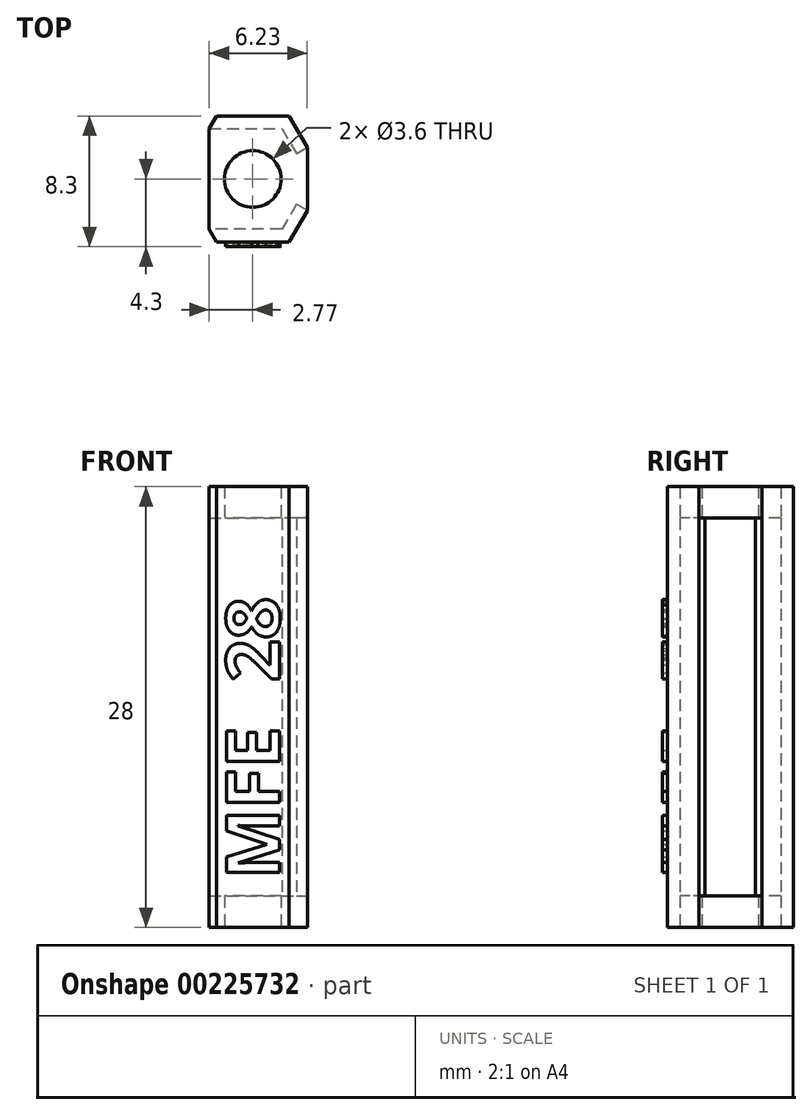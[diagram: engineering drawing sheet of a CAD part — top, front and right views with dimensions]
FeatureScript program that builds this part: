
annotation { "Feature Type Name" : "Feature", "Feature Type Description" : "" }
export const myFeature = defineFeature(function(context is Context, id is Id, definition is map)
    precondition{}
    {
        {
            assignVariable(context, id + "F0", {"name" : "Hex_Nut", "anyValue" : 6.4});
        }
        {
            assignVariable(context, id + "F1", {"name" : "Wall_thick", "anyValue" : 0.8});
        }
        {
            assignVariable(context, id + "F2", {"name" : "Stand_Height", "anyValue" : 28});
        }
        {
            var Q0;
            Q0=qCreatedBy(makeId("Top.planeOp"),FACE);
            var sketch = newSketch(context, id + "F3", { "sketchPlane" : qUnion([Q0])});
            skCircle(sketch, "E0.cCircle", {"center": v(0, 0) * mm, "radius": 4 * mm, "construction": true});
            skLineSegment(sketch, "E0.0", {"start": v(-2.3, 4) * mm, "end": v(2.3, 4) * mm});
            skLineSegment(sketch, "E0.1", {"start": v(2.3, 4) * mm, "end": v(3.46, 2) * mm});
            skLineSegment(sketch, "E0.2", {"start": v(3.46, -2) * mm, "end": v(2.3, -4) * mm});
            skLineSegment(sketch, "E0.3", {"start": v(2.3, -4) * mm, "end": v(-2.3, -4) * mm});
            skLineSegment(sketch, "E0.4", {"start": v(-2.3, -4) * mm, "end": v(-2.77, -3.2) * mm});
            skLineSegment(sketch, "E0.5", {"start": v(-2.77, 3.2) * mm, "end": v(-2.3, 4) * mm});
            skPoint(sketch, "E0.0.midPoint", {"position": v(0, 4) * mm});
            skCircle(sketch, "E1", {"center": v(0, 0) * mm, "radius": 1.8 * mm, "construction": true});
            skLineSegment(sketch, "E2", {"start": v(-2.77, 3.2) * mm, "end": v(-2.77, -3.2) * mm});
            skLineSegment(sketch, "E3", {"start": v(3.46, 2) * mm, "end": v(3.46, -2) * mm});
            skPoint(sketch, "E4.orphan", {"position": v(-4.62, 0) * mm});
            skPoint(sketch, "E5.orphan", {"position": v(4.62, 0) * mm});
            skSolve(sketch);
        }
        {
            var Q0;
            Q0=qCreatedBy(makeId("Top.planeOp"),FACE);
            var sketch = newSketch(context, id + "F4", { "sketchPlane" : qUnion([Q0])});
            skCircle(sketch, "E6.cCircle", {"center": v(0, 0) * mm, "radius": 3.2 * mm, "construction": true});
            skLineSegment(sketch, "E6.0", {"start": v(-5, 3.2) * mm, "end": v(1.85, 3.2) * mm});
            skLineSegment(sketch, "E6.1", {"start": v(1.85, 3.2) * mm, "end": v(2.77, 1.6) * mm});
            skLineSegment(sketch, "E6.2", {"start": v(2.77, -1.6) * mm, "end": v(1.85, -3.2) * mm});
            skLineSegment(sketch, "E6.3", {"start": v(1.85, -3.2) * mm, "end": v(-5, -3.2) * mm});
            skLineSegment(sketch, "E6.4", {"start": v(-1.85, -3.2) * mm, "end": v(-3.7, 0) * mm, "construction": true});
            skLineSegment(sketch, "E6.5", {"start": v(-3.7, 0) * mm, "end": v(-1.85, 3.2) * mm, "construction": true});
            skPoint(sketch, "E6.0.midPoint", {"position": v(0, 3.2) * mm});
            skLineSegment(sketch, "E7", {"start": v(2.77, 1.6) * mm, "end": v(5, 2.89) * mm});
            skLineSegment(sketch, "E8", {"start": v(5, 2.89) * mm, "end": v(5, -2.89) * mm});
            skLineSegment(sketch, "E9", {"start": v(5, -2.89) * mm, "end": v(2.77, -1.6) * mm});
            skLineSegment(sketch, "E10", {"start": v(-5, 3.2) * mm, "end": v(-5, -3.2) * mm});
            skPoint(sketch, "E11.orphan", {"position": v(3.7, 0) * mm});
            skSolve(sketch);
        }
        {
            var Q0;
            Q0=qCreatedBy(makeId("Top.planeOp"),FACE);
            var sketch = newSketch(context, id + "F5", { "sketchPlane" : qUnion([Q0])});
            skCircle(sketch, "E12", {"center": v(0, 0) * mm, "radius": 1.8 * mm});
            skSolve(sketch);
        }
        {
            var Q0;
            Q0=qSketchRegion(id+"F3",true);
            extrude(context, id + "F6", {"entities" : qUnion([Q0]), "endBound" : BoundingType.SYMMETRIC, "depth" : (getVariable(context, 'Stand_Height')) * mm});
        }
        {
            var Q0;
            Q0=qSketchRegion(id+"F4",true);
            extrude(context, id + "F7", {"entities" : qUnion([Q0]), "operationType" : NewBodyOperationType.REMOVE, "endBound" : BoundingType.SYMMETRIC, "depth" : (getVariable(context, 'Stand_Height') - 4) * mm});
        }
        {
            var Q0;
            Q0=qSketchRegion(id+"F5",true);
            extrude(context, id + "F8", {"entities" : qUnion([Q0]), "operationType" : NewBodyOperationType.REMOVE, "endBound" : BoundingType.SYMMETRIC, "depth" : (getVariable(context, 'Stand_Height')) * mm});
        }
        {
            var Q0;
            Q0=qCreatedBy(makeId("Front.planeOp"),FACE);
            var sketch = newSketch(context, id + "F9", { "sketchPlane" : qUnion([Q0])});
            skText(sketch, "E13", { "text": "MFE", "fontName": "OpenSans-Bold.ttf"});
            skLineSegment(sketch, "E14", {"start": v(0, 0) * mm, "end": v(0, -1.2) * mm, "construction": true});
            const initialGuessF9  = {"E13": [0.0017, -0.01092, 0, 1, 0.0034]};
            skSetInitialGuess(sketch, initialGuessF9);
            skSolve(sketch);
        }
        {
            var Q0;
            Q0=qSketchRegion(id+"F9",true);
            extrude(context, id + "F10", {"entities" : qUnion([Q0]), "operationType" : NewBodyOperationType.ADD, "depth" : ((getVariable(context, 'Hex_Nut') / 2) + getVariable(context, 'Wall_thick') + 0.3) * mm, "hasSecondDirection" : true, "secondDirectionOppositeDirection" : false, "secondDirectionDepth" : ((getVariable(context, 'Hex_Nut') / 2) + 0.2) * mm});
        }
        {
            var Q0;
            Q0=qCreatedBy(makeId("Front.planeOp"),FACE);
            var sketch = newSketch(context, id + "F11", { "sketchPlane" : qUnion([Q0])});
            skText(sketch, "E15", { "text": "28", "fontName": "OpenSans-Bold.ttf"});
            skLineSegment(sketch, "E16", {"start": v(0, 0) * mm, "end": v(0, 1.6) * mm, "construction": true});
            const initialGuessF11  = {"E15": [0.0017, 0.0016, 0, 1, 0.0034]};
            skSetInitialGuess(sketch, initialGuessF11);
            skSolve(sketch);
        }
        {
            var Q0;
            Q0=qSketchRegion(id+"F11",true);
            var Q1;
            Q1=makeQuery(id+"F10.opExtrude","CAP_FACE",FACE,{"disambiguationData":[OSD([sQuery(id+"F9.wireOp",EDGE,"E13.sketch_text.stroke-29"),sQuery(id+"F9.wireOp",EDGE,"E13.sketch_text.stroke-30"),sQuery(id+"F9.wireOp",EDGE,"E13.sketch_text.stroke-31"),sQuery(id+"F9.wireOp",EDGE,"E13.sketch_text.stroke-32"),sQuery(id+"F9.wireOp",EDGE,"E13.sketch_text.stroke-33"),sQuery(id+"F9.wireOp",EDGE,"E13.sketch_text.stroke-34"),sQuery(id+"F9.wireOp",EDGE,"E13.sketch_text.stroke-35"),sQuery(id+"F9.wireOp",EDGE,"E13.sketch_text.stroke-36"),sQuery(id+"F9.wireOp",EDGE,"E13.sketch_text.stroke-37"),sQuery(id+"F9.wireOp",EDGE,"E13.sketch_text.stroke-38"),sQuery(id+"F9.wireOp",EDGE,"E13.sketch_text.stroke-39"),sQuery(id+"F9.wireOp",EDGE,"E13.sketch_text.stroke-40")])],"isStart":false});
            var Q2;
            Q2=makeQuery(id+"F7.boolean.opBoolean","COPY",FACE,{"derivedFrom":makeQuery(id+"F7.opExtrude","SWEPT_FACE",FACE,{"disambiguationData":[OSD([sQuery(id+"F4.wireOp",EDGE,"E6.3")])]})});
            extrude(context, id + "F12", {"entities" : qUnion([Q0]), "operationType" : NewBodyOperationType.ADD, "endBound" : BoundingType.UP_TO_SURFACE, "endBoundEntityFace" : qUnion([Q1]), "depth" : ((getVariable(context, 'Hex_Nut') / 2) + getVariable(context, 'Wall_thick') + 0.3) * mm, "hasSecondDirection" : true, "secondDirectionBound" : SecondDirectionBoundingType.UP_TO_SURFACE, "secondDirectionOppositeDirection" : false, "secondDirectionBoundEntityFace" : qUnion([Q2]), "secondDirectionDepth" : 25 * mm});
        }
    });
